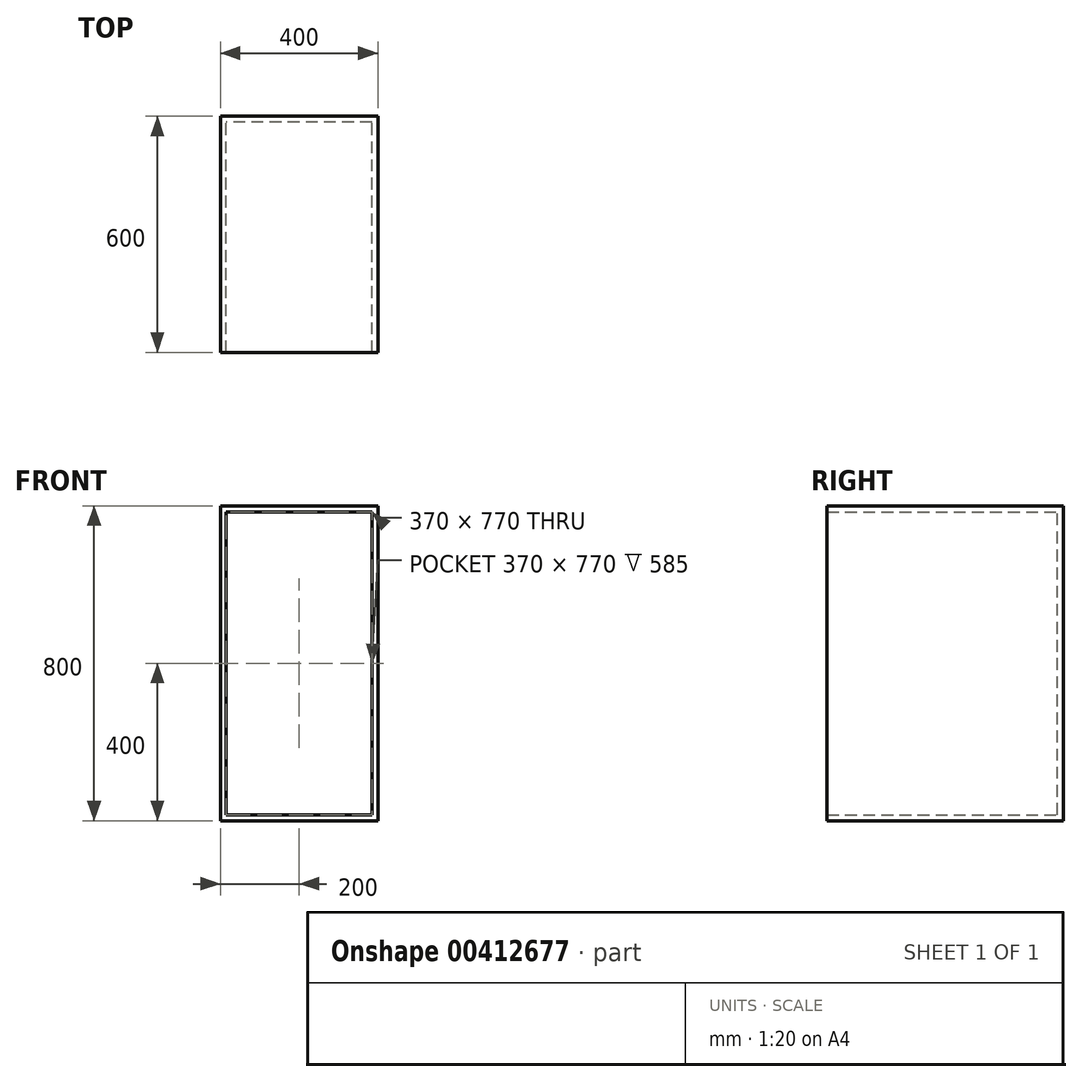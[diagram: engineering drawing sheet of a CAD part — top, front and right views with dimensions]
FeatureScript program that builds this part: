
annotation { "Feature Type Name" : "Feature", "Feature Type Description" : "" }
export const myFeature = defineFeature(function(context is Context, id is Id, definition is map)
    precondition{}
    {
        {
            var Q0;
            Q0=qCreatedBy(makeId("Right.planeOp"),FACE);
            var sketch = newSketch(context, id + "F0", { "sketchPlane" : qUnion([Q0])});
            skLineSegment(sketch, "E0.bottom", {"start": v(0, 0) * mm, "end": v(600, 0) * mm});
            skLineSegment(sketch, "E0.top", {"start": v(0, 800) * mm, "end": v(600, 800) * mm});
            skLineSegment(sketch, "E0.left", {"start": v(0, 0) * mm, "end": v(0, 800) * mm});
            skLineSegment(sketch, "E0.right", {"start": v(600, 0) * mm, "end": v(600, 800) * mm});
            skSolve(sketch);
        }
        {
            var Q0;
            Q0=makeQuery(id+"F0.imprint","IMPRINT",FACE,{"disambiguationData":[TD([[makeQuery(id+"F0.imprint","IMPRINT",EDGE,{"derivedFrom":sQuery(id+"F0.wireOp",EDGE,"E0.bottom")}),1.0]])]});
            extrude(context, id + "F1", {"entities" : qUnion([Q0]), "depth" : 400 * mm});
        }
        {
            var Q0;
            Q0=makeQuery(id+"F1.opExtrude","SWEPT_FACE",FACE,{"disambiguationData":[OSD([sQuery(id+"F0.wireOp",EDGE,"E0.left")])]});
            shell(context, id + "F2", {"entities" : qUnion([Q0]), "thickness" : 15 * mm});
        }
    });
